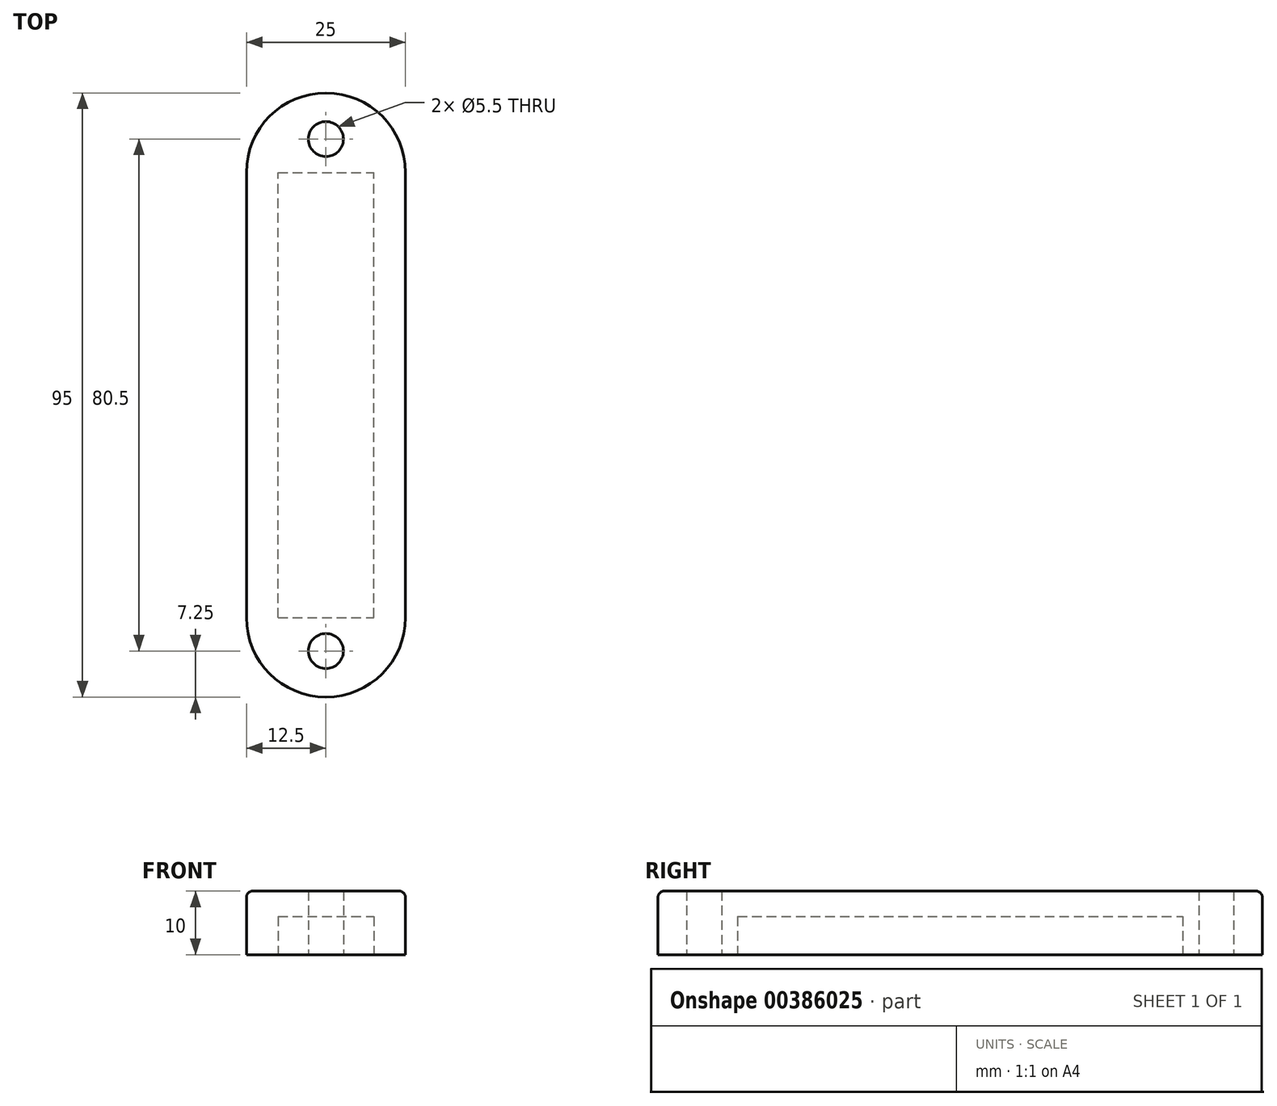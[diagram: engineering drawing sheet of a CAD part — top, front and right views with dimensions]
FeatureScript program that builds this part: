
annotation { "Feature Type Name" : "Feature", "Feature Type Description" : "" }
export const myFeature = defineFeature(function(context is Context, id is Id, definition is map)
    precondition{}
    {
        {
            var Q0;
            Q0=qCreatedBy(makeId("Top.planeOp"),FACE);
            var sketch = newSketch(context, id + "F0", { "sketchPlane" : qUnion([Q0])});
            skLineSegment(sketch, "E0.bottom", {"start": v(0, 0) * mm, "end": v(25, 0) * mm});
            skLineSegment(sketch, "E0.top", {"start": v(0, 95) * mm, "end": v(25, 95) * mm});
            skLineSegment(sketch, "E0.left", {"start": v(0, 0) * mm, "end": v(0, 95) * mm});
            skLineSegment(sketch, "E0.right", {"start": v(25, 0) * mm, "end": v(25, 95) * mm});
            skPoint(sketch, "E1", {"position": v(12.5, 87.75) * mm});
            skPoint(sketch, "E1.positionSnap0", {"position": v(12.5, 95) * mm});
            skPoint(sketch, "E2", {"position": v(12.5, 7.25) * mm});
            skPoint(sketch, "E2.positionSnap0", {"position": v(12.5, 0) * mm});
            skCircle(sketch, "E3", {"center": v(12.5, 87.75) * mm, "radius": 2.75 * mm});
            skCircle(sketch, "E4", {"center": v(12.5, 7.25) * mm, "radius": 2.75 * mm});
            skSolve(sketch);
        }
        {
            var Q0;
            Q0 = qSketchRegion(id + "F0", true);
            extrude(context, id + "F1", {"entities" : qUnion([Q0]), "depth" : 10 * mm});
        }
        {
            var Q0;
            Q0=makeQuery(id+"F1.opExtrude","SWEPT_EDGE",EDGE,{"disambiguationData":[OSD([sQuery(id+"F0.wireOp",EDGE,"E0.top"),sQuery(id+"F0.wireOp",EDGE,"E0.right")])]});
            var Q1;
            Q1=makeQuery(id+"F1.opExtrude","SWEPT_EDGE",EDGE,{"disambiguationData":[OSD([sQuery(id+"F0.wireOp",EDGE,"E0.top"),sQuery(id+"F0.wireOp",EDGE,"E0.left")])]});
            var Q2;
            Q2=makeQuery(id+"F1.opExtrude","SWEPT_EDGE",EDGE,{"disambiguationData":[OSD([sQuery(id+"F0.wireOp",EDGE,"E0.bottom"),sQuery(id+"F0.wireOp",EDGE,"E0.right")])]});
            var Q3;
            Q3=makeQuery(id+"F1.opExtrude","SWEPT_EDGE",EDGE,{"disambiguationData":[OSD([sQuery(id+"F0.wireOp",EDGE,"E0.bottom"),sQuery(id+"F0.wireOp",EDGE,"E0.left")])]});
            fillet(context, id + "F2", {"entities" : qUnion([Q0, Q1, Q2, Q3]), "radius" : 12.5 * mm, "tangentPropagation" : true, "allowEdgeOverflow" : false});
        }
        {
            var Q0;
            Q0=makeQuery(id+"F1.opExtrude","CAP_EDGE",EDGE,{"disambiguationData":[OSD([sQuery(id+"F0.wireOp",EDGE,"E0.right")])],"isStart":false});
            var Q1;
            Q1=makeQuery(id+"F1.opExtrude","CAP_EDGE",EDGE,{"disambiguationData":[OSD([sQuery(id+"F0.wireOp",EDGE,"E0.left")])],"isStart":false});
            var Q2;
            Q2=makeQuery(id+"F1.opExtrude","CAP_EDGE",EDGE,{"disambiguationData":[OSD([sQuery(id+"F0.wireOp",EDGE,"E0.top")])],"isStart":false});
            var Q3;
            {var subQ0=sQuery(id+"F0.wireOp",EDGE,"E0.right");var subQ1=sQuery(id+"F0.wireOp",EDGE,"E0.top");Q3=makeQuery(id+"F2.opFillet","BLEND_EDGE",EDGE,{"blendedFrom":[makeQuery(id+"F1.opExtrude","SWEPT_EDGE",EDGE,{"disambiguationData":[OSD([subQ1,subQ0])]}),makeQuery(id+"F1.opExtrude","CAP_FACE",FACE,{"disambiguationData":[OSD([sQuery(id+"F0.wireOp",EDGE,"E0.bottom"),subQ1,sQuery(id+"F0.wireOp",EDGE,"E0.left"),subQ0,sQuery(id+"F0.wireOp",EDGE,"E3"),sQuery(id+"F0.wireOp",EDGE,"E4")])],"isStart":false})],"blendedInto":[makeQuery(id+"F1.opExtrude","CAP_FACE",FACE,{"disambiguationData":[OSD([sQuery(id+"F0.wireOp",EDGE,"E0.bottom"),subQ1,sQuery(id+"F0.wireOp",EDGE,"E0.left"),subQ0,sQuery(id+"F0.wireOp",EDGE,"E3"),sQuery(id+"F0.wireOp",EDGE,"E4")])],"isStart":false})]});}
            var Q4;
            {var subQ0=sQuery(id+"F0.wireOp",EDGE,"E0.left");var subQ1=sQuery(id+"F0.wireOp",EDGE,"E0.top");Q4=makeQuery(id+"F2.opFillet","BLEND_EDGE",EDGE,{"blendedFrom":[makeQuery(id+"F1.opExtrude","SWEPT_EDGE",EDGE,{"disambiguationData":[OSD([subQ1,subQ0])]}),makeQuery(id+"F1.opExtrude","CAP_FACE",FACE,{"disambiguationData":[OSD([sQuery(id+"F0.wireOp",EDGE,"E0.bottom"),subQ1,subQ0,sQuery(id+"F0.wireOp",EDGE,"E0.right"),sQuery(id+"F0.wireOp",EDGE,"E3"),sQuery(id+"F0.wireOp",EDGE,"E4")])],"isStart":false})],"blendedInto":[makeQuery(id+"F1.opExtrude","CAP_FACE",FACE,{"disambiguationData":[OSD([sQuery(id+"F0.wireOp",EDGE,"E0.bottom"),subQ1,subQ0,sQuery(id+"F0.wireOp",EDGE,"E0.right"),sQuery(id+"F0.wireOp",EDGE,"E3"),sQuery(id+"F0.wireOp",EDGE,"E4")])],"isStart":false})]});}
            var Q5;
            {var subQ0=sQuery(id+"F0.wireOp",EDGE,"E0.right");var subQ1=sQuery(id+"F0.wireOp",EDGE,"E0.bottom");Q5=makeQuery(id+"F2.opFillet","BLEND_EDGE",EDGE,{"blendedFrom":[makeQuery(id+"F1.opExtrude","SWEPT_EDGE",EDGE,{"disambiguationData":[OSD([subQ1,subQ0])]}),makeQuery(id+"F1.opExtrude","CAP_FACE",FACE,{"disambiguationData":[OSD([subQ1,sQuery(id+"F0.wireOp",EDGE,"E0.top"),sQuery(id+"F0.wireOp",EDGE,"E0.left"),subQ0,sQuery(id+"F0.wireOp",EDGE,"E3"),sQuery(id+"F0.wireOp",EDGE,"E4")])],"isStart":false})],"blendedInto":[makeQuery(id+"F1.opExtrude","CAP_FACE",FACE,{"disambiguationData":[OSD([subQ1,sQuery(id+"F0.wireOp",EDGE,"E0.top"),sQuery(id+"F0.wireOp",EDGE,"E0.left"),subQ0,sQuery(id+"F0.wireOp",EDGE,"E3"),sQuery(id+"F0.wireOp",EDGE,"E4")])],"isStart":false})]});}
            var Q6;
            Q6=makeQuery(id+"F1.opExtrude","CAP_EDGE",EDGE,{"disambiguationData":[OSD([sQuery(id+"F0.wireOp",EDGE,"E0.bottom")])],"isStart":false});
            var Q7;
            {var subQ0=sQuery(id+"F0.wireOp",EDGE,"E0.left");var subQ1=sQuery(id+"F0.wireOp",EDGE,"E0.bottom");Q7=makeQuery(id+"F2.opFillet","BLEND_EDGE",EDGE,{"blendedFrom":[makeQuery(id+"F1.opExtrude","SWEPT_EDGE",EDGE,{"disambiguationData":[OSD([subQ1,subQ0])]}),makeQuery(id+"F1.opExtrude","CAP_FACE",FACE,{"disambiguationData":[OSD([subQ1,sQuery(id+"F0.wireOp",EDGE,"E0.top"),subQ0,sQuery(id+"F0.wireOp",EDGE,"E0.right"),sQuery(id+"F0.wireOp",EDGE,"E3"),sQuery(id+"F0.wireOp",EDGE,"E4")])],"isStart":false})],"blendedInto":[makeQuery(id+"F1.opExtrude","CAP_FACE",FACE,{"disambiguationData":[OSD([subQ1,sQuery(id+"F0.wireOp",EDGE,"E0.top"),subQ0,sQuery(id+"F0.wireOp",EDGE,"E0.right"),sQuery(id+"F0.wireOp",EDGE,"E3"),sQuery(id+"F0.wireOp",EDGE,"E4")])],"isStart":false})]});}
            fillet(context, id + "F3", {"entities" : qUnion([Q0, Q1, Q2, Q3, Q4, Q5, Q6, Q7]), "radius" : 1 * mm, "tangentPropagation" : true, "allowEdgeOverflow" : false});
        }
        {
            var Q0;
            Q0=makeQuery(id+"F1.opExtrude","CAP_FACE",FACE,{"disambiguationData":[OSD([sQuery(id+"F0.wireOp",EDGE,"E0.bottom"),sQuery(id+"F0.wireOp",EDGE,"E0.top"),sQuery(id+"F0.wireOp",EDGE,"E0.left"),sQuery(id+"F0.wireOp",EDGE,"E0.right"),sQuery(id+"F0.wireOp",EDGE,"E3"),sQuery(id+"F0.wireOp",EDGE,"E4")])],"isStart":true});
            var sketch = newSketch(context, id + "F4", { "sketchPlane" : qUnion([Q0])});
            skLineSegment(sketch, "E5.bottom", {"start": v(5, -12.5) * mm, "end": v(20, -12.5) * mm});
            skLineSegment(sketch, "E5.top", {"start": v(5, -82.5) * mm, "end": v(20, -82.5) * mm});
            skLineSegment(sketch, "E5.left", {"start": v(5, -12.5) * mm, "end": v(5, -82.5) * mm});
            skLineSegment(sketch, "E5.right", {"start": v(20, -12.5) * mm, "end": v(20, -82.5) * mm});
            skSolve(sketch);
        }
        {
            var Q0;
            Q0 = qSketchRegion(id + "F4", true);
            extrude(context, id + "F5", {"entities" : qUnion([Q0]), "operationType" : NewBodyOperationType.REMOVE, "oppositeDirection" : true, "depth" : 6 * mm});
        }
    });
